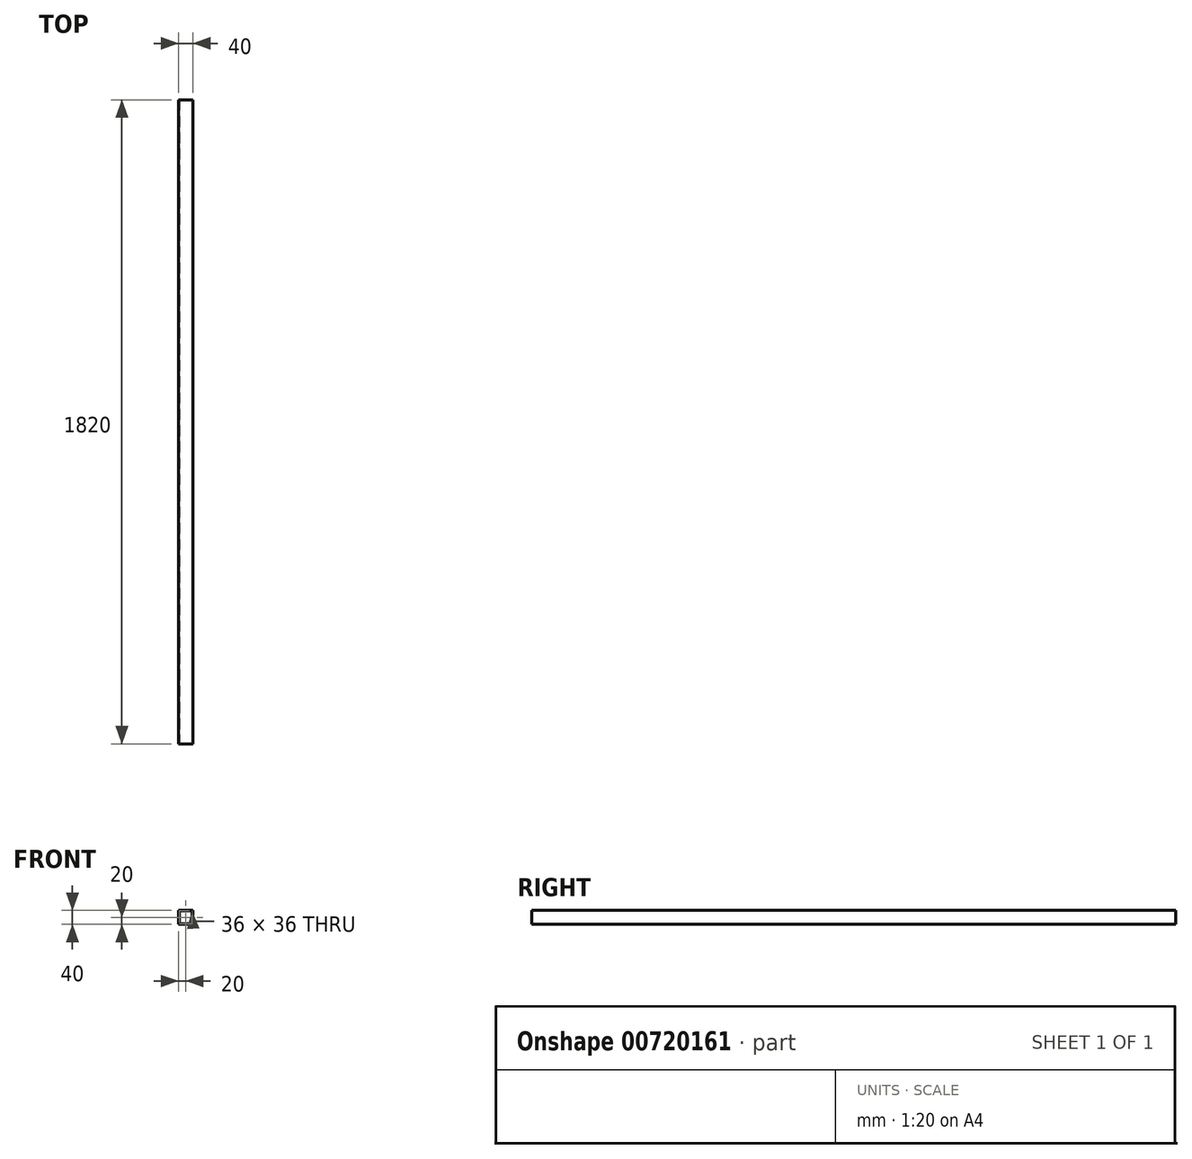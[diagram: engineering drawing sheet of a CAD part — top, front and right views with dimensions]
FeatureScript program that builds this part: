
annotation { "Feature Type Name" : "Feature", "Feature Type Description" : "" }
export const myFeature = defineFeature(function(context is Context, id is Id, definition is map)
    precondition{}
    {
        {
            var Q0;
            Q0=qCreatedBy(makeId("Front.planeOp"),FACE);
            var sketch = newSketch(context, id + "F0", { "sketchPlane" : qUnion([Q0])});
            skLineSegment(sketch, "E0.bottom", {"start": v(0, 0) * mm, "end": v(40, 0) * mm});
            skLineSegment(sketch, "E0.top", {"start": v(0, 40) * mm, "end": v(40, 40) * mm});
            skLineSegment(sketch, "E0.left", {"start": v(0, 0) * mm, "end": v(0, 40) * mm});
            skLineSegment(sketch, "E0.right", {"start": v(40, 0) * mm, "end": v(40, 40) * mm});
            skSolve(sketch);
        }
        {
            var Q0;
            Q0=qSketchRegion(id+"F0",true);
            extrude(context, id + "F1", {"entities" : qUnion([Q0]), "depth" : 1820 * mm, "offsetDistance" : 25 * mm});
        }
        {
            var Q0;
            Q0=makeQuery(id+"F1.opExtrude","CAP_FACE",FACE,{"disambiguationData":[OSD([sQuery(id+"F0.wireOp",EDGE,"E0.bottom"),sQuery(id+"F0.wireOp",EDGE,"E0.top"),sQuery(id+"F0.wireOp",EDGE,"E0.left"),sQuery(id+"F0.wireOp",EDGE,"E0.right")])],"isStart":false});
            var sketch = newSketch(context, id + "F2", { "sketchPlane" : qUnion([Q0])});
            skLineSegment(sketch, "E1.bottom", {"start": v(2, 2) * mm, "end": v(38, 2) * mm});
            skLineSegment(sketch, "E1.top", {"start": v(2, 38) * mm, "end": v(38, 38) * mm});
            skLineSegment(sketch, "E1.left", {"start": v(2, 2) * mm, "end": v(2, 38) * mm});
            skLineSegment(sketch, "E1.right", {"start": v(38, 2) * mm, "end": v(38, 38) * mm});
            skSolve(sketch);
        }
        {
            var Q0;
            Q0=makeQuery(id+"F2.imprint","IMPRINT",FACE,{"disambiguationData":[TD([[makeQuery(id+"F2.imprint","IMPRINT",EDGE,{"derivedFrom":sQuery(id+"F2.wireOp",EDGE,"E1.bottom")}),1.0]])]});
            extrude(context, id + "F3", {"entities" : qUnion([Q0]), "operationType" : NewBodyOperationType.REMOVE, "endBound" : BoundingType.THROUGH_ALL, "oppositeDirection" : true, "depth" : 25 * mm, "offsetDistance" : 25 * mm});
        }
    });
